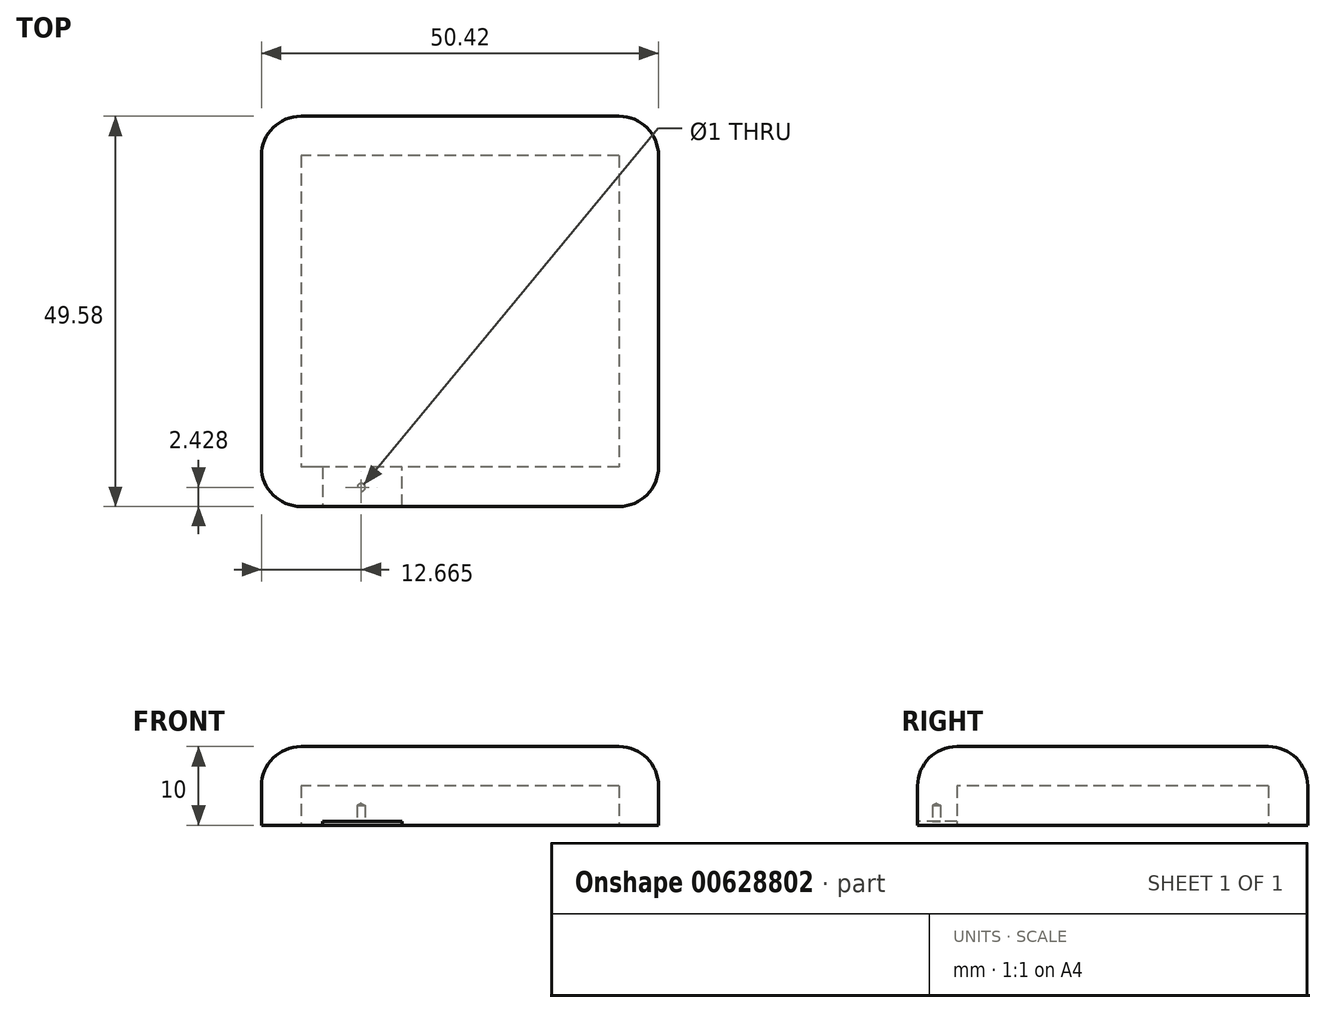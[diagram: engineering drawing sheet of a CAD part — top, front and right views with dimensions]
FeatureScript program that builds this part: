
annotation { "Feature Type Name" : "Feature", "Feature Type Description" : "" }
export const myFeature = defineFeature(function(context is Context, id is Id, definition is map)
    precondition{}
    {
        {
            var Q0;
            Q0=qCreatedBy(makeId("Top.planeOp"),FACE);
            var sketch = newSketch(context, id + "F0", { "sketchPlane" : qUnion([Q0])});
            skLineSegment(sketch, "E0.bottom", {"start": v(25.21, 24.79) * mm, "end": v(-25.21, 24.79) * mm});
            skLineSegment(sketch, "E0.top", {"start": v(25.21, -24.79) * mm, "end": v(-25.21, -24.79) * mm});
            skLineSegment(sketch, "E0.left", {"start": v(25.21, 24.79) * mm, "end": v(25.21, -24.79) * mm});
            skLineSegment(sketch, "E0.right", {"start": v(-25.21, 24.79) * mm, "end": v(-25.21, -24.79) * mm});
            skPoint(sketch, "E0.middle", {"position": v(0, 0) * mm});
            skSolve(sketch);
        }
        {
            var Q0;
            Q0 = qSketchRegion(id + "F0", true);
            extrude(context, id + "F1", {"entities" : qUnion([Q0]), "depth" : 10 * mm, "offsetDistance" : 25 * mm});
        }
        {
            var Q0;
            Q0=makeQuery(id+"F1.opExtrude","CAP_FACE",FACE,{"disambiguationData":[OSD([sQuery(id+"F0.wireOp",EDGE,"E0.bottom"),sQuery(id+"F0.wireOp",EDGE,"E0.top"),sQuery(id+"F0.wireOp",EDGE,"E0.left"),sQuery(id+"F0.wireOp",EDGE,"E0.right")])],"isStart":true});
            shell(context, id + "F2", {"entities" : qUnion([Q0]), "thickness" : 5 * mm});
        }
        {
            var Q0;
            Q0=makeQuery(id+"F1.opExtrude","CAP_FACE",FACE,{"disambiguationData":[OSD([sQuery(id+"F0.wireOp",EDGE,"E0.bottom"),sQuery(id+"F0.wireOp",EDGE,"E0.top"),sQuery(id+"F0.wireOp",EDGE,"E0.left"),sQuery(id+"F0.wireOp",EDGE,"E0.right")])],"isStart":true});
            var sketch = newSketch(context, id + "F3", { "sketchPlane" : qUnion([Q0])});
            skLineSegment(sketch, "E1", {"start": v(-20.21, 19.79) * mm, "end": v(-17.48, 19.79) * mm});
            skLineSegment(sketch, "E2", {"start": v(-17.48, 19.79) * mm, "end": v(-17.48, 24.79) * mm});
            skLineSegment(sketch, "E3", {"start": v(-17.48, 24.79) * mm, "end": v(-7.37, 24.79) * mm});
            skLineSegment(sketch, "E4", {"start": v(-7.37, 24.79) * mm, "end": v(-7.37, 19.79) * mm});
            skLineSegment(sketch, "E5", {"start": v(-7.37, 19.79) * mm, "end": v(-17.48, 19.79) * mm});
            skSolve(sketch);
        }
        {
            var Q0;
            Q0=makeQuery(id+"F3.imprint","IMPRINT",FACE,{"disambiguationData":[TD([[makeQuery(id+"F3.imprint","IMPRINT",EDGE,{"derivedFrom":sQuery(id+"F3.wireOp",EDGE,"E2")}),-1.0]])]});
            extrude(context, id + "F4", {"entities" : qUnion([Q0]), "operationType" : NewBodyOperationType.REMOVE, "oppositeDirection" : true, "depth" : .5 * mm, "offsetDistance" : 25 * mm});
        }
        {
            var Q0;
            Q0=makeQuery(id+"F4.boolean.opBoolean","COPY",FACE,{"derivedFrom":makeQuery(id+"F4.opExtrude","CAP_FACE",FACE,{"disambiguationData":[OSD([sQuery(id+"F3.wireOp",EDGE,"E2"),sQuery(id+"F3.wireOp",EDGE,"E3"),sQuery(id+"F3.wireOp",EDGE,"E4"),sQuery(id+"F3.wireOp",EDGE,"E5")])],"isStart":false})});
            var sketch = newSketch(context, id + "F5", { "sketchPlane" : qUnion([Q0])});
            skSolve(sketch);
        }
        {
            var Q0;
            Q0=makeQuery(id+"F5.imprint","IMPRINT",FACE,{"disambiguationData":[TD([[makeQuery(id+"F5.imprint","IMPRINT",EDGE,{"derivedFrom":makeQuery(id+"F4.boolean.opBoolean","COPY",EDGE,{"derivedFrom":makeQuery(id+"F4.opExtrude","CAP_EDGE",EDGE,{"disambiguationData":[OSD([sQuery(id+"F3.wireOp",EDGE,"E2")])],"isStart":false})})}),-1.0]])]});
            var sketch = newSketch(context, id + "F6", { "sketchPlane" : qUnion([Q0])});
            skPoint(sketch, "E6", {"position": v(-12.54, 22.36) * mm});
            skSolve(sketch);
        }
        {
            var Q0;
            Q0=sQuery(id+"FF0PB6D72XfAnTP_1.wireOp",VERTEX,"f734cbfc-d673-42cc-b759-daba2a504a01");
            var Q1;
            Q1=sQuery(id+"F6.wireOp",VERTEX,"E6");
            var Q2;
            Q2=makeQuery(id+"F1.opExtrude","SWEPT_BODY",BODY,{"disambiguationData":[OSD([sQuery(id+"F0.wireOp",EDGE,"E0.bottom"),sQuery(id+"F0.wireOp",EDGE,"E0.top"),sQuery(id+"F0.wireOp",EDGE,"E0.left"),sQuery(id+"F0.wireOp",EDGE,"E0.right")])]});
            hole(context, id + "F7", {"style" : HoleStyle.SIMPLE, "endStyle" : HoleEndStyle.BLIND, "holeDiameter" : 1 * mm, "majorDiameter" : 5 * mm, "holeDepth" : 2 * mm, "isTappedThrough" : true, "tappedDepth" : 12 * mm, "tapClearance" : 3, "locations" : qUnion([Q0, Q1]), "scope" : qUnion([Q2])});
        }
        {
            var Q0;
            Q0=makeQuery(id+"F1.opExtrude","SWEPT_EDGE",EDGE,{"disambiguationData":[OSD([sQuery(id+"F0.wireOp",EDGE,"E0.top"),sQuery(id+"F0.wireOp",EDGE,"E0.right")])]});
            var Q1;
            Q1=makeQuery(id+"F1.opExtrude","SWEPT_EDGE",EDGE,{"disambiguationData":[OSD([sQuery(id+"F0.wireOp",EDGE,"E0.top"),sQuery(id+"F0.wireOp",EDGE,"E0.left")])]});
            var Q2;
            Q2=makeQuery(id+"F1.opExtrude","SWEPT_EDGE",EDGE,{"disambiguationData":[OSD([sQuery(id+"F0.wireOp",EDGE,"E0.bottom"),sQuery(id+"F0.wireOp",EDGE,"E0.left")])]});
            var Q3;
            Q3=makeQuery(id+"F1.opExtrude","SWEPT_EDGE",EDGE,{"disambiguationData":[OSD([sQuery(id+"F0.wireOp",EDGE,"E0.bottom"),sQuery(id+"F0.wireOp",EDGE,"E0.right")])]});
            fillet(context, id + "F8", {"entities" : qUnion([Q0, Q1, Q2, Q3]), "radius" : 5 * mm, "tangentPropagation" : true, "allowEdgeOverflow" : false});
        }
        {
            var Q0;
            Q0=makeQuery(id+"F1.opExtrude","CAP_FACE",FACE,{"disambiguationData":[OSD([sQuery(id+"F0.wireOp",EDGE,"E0.bottom"),sQuery(id+"F0.wireOp",EDGE,"E0.top"),sQuery(id+"F0.wireOp",EDGE,"E0.left"),sQuery(id+"F0.wireOp",EDGE,"E0.right")])],"isStart":false});
            fillet(context, id + "F9", {"entities" : qUnion([Q0]), "radius" : 5 * mm, "tangentPropagation" : true, "allowEdgeOverflow" : false});
        }
    });
